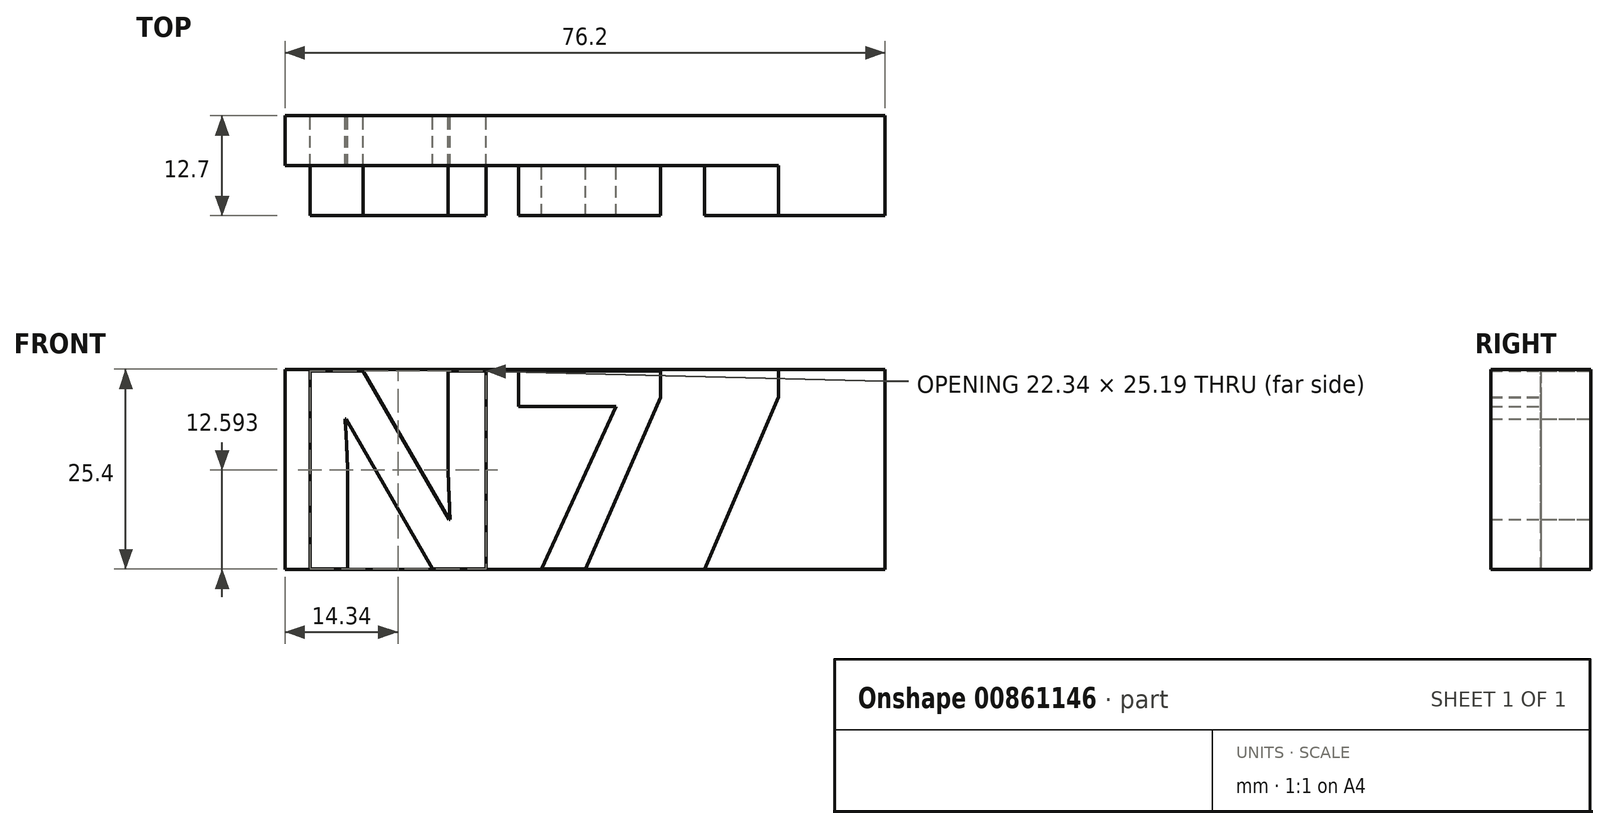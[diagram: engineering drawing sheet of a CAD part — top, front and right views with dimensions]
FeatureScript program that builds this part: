
annotation { "Feature Type Name" : "Feature", "Feature Type Description" : "" }
export const myFeature = defineFeature(function(context is Context, id is Id, definition is map)
    precondition{}
    {
        {
            var Q0;
            Q0=qCreatedBy(makeId("Front.planeOp"),FACE);
            var sketch = newSketch(context, id + "F0", { "sketchPlane" : qUnion([Q0])});
            skText(sketch, "E0", { "text": "N7", "fontName": "OpenSans-Bold.ttf"});
            skLineSegment(sketch, "E1.bottom", {"start": v(-29.76, 111.46) * mm, "end": v(46.44, 111.46) * mm});
            skLineSegment(sketch, "E1.top", {"start": v(-29.76, 86.06) * mm, "end": v(46.44, 86.06) * mm});
            skLineSegment(sketch, "E1.left", {"start": v(-29.76, 111.46) * mm, "end": v(-29.76, 86.06) * mm});
            skLineSegment(sketch, "E1.right", {"start": v(46.44, 111.46) * mm, "end": v(46.44, 86.06) * mm});
            skLineSegment(sketch, "E2", {"start": v(20.22, 111.46) * mm, "end": v(32.92, 111.46) * mm});
            skLineSegment(sketch, "E3", {"start": v(32.92, 111.46) * mm, "end": v(32.92, 107.96) * mm});
            skLineSegment(sketch, "E4", {"start": v(23.41, 85.79) * mm, "end": v(32.92, 107.96) * mm});
            skLineSegment(sketch, "E5", {"start": v(20.22, 86.06) * mm, "end": v(23.41, 85.79) * mm});
            const initialGuessF0  = {"E0": [-0.02976, 0.08606, 1, 0, 0.0254]};
            skSetInitialGuess(sketch, initialGuessF0);
            skSolve(sketch);
        }
        {
            var Q0;
            {var subQ1=sQuery(id+"F0.wireOp",EDGE,"E0.sketch_text.stroke-1");Q0=makeQuery(id+"F0.imprint","IMPRINT",FACE,{"disambiguationData":[TD([[makeQuery(id+"F0.imprint","IMPRINT",EDGE,{"derivedFrom":subQ1}),1.0]])]});}
            var Q1;
            {var subQ5=sQuery(id+"F0.wireOp",EDGE,"E0.sketch_text.stroke-6");Q1=makeQuery(id+"F0.imprint","IMPRINT",FACE,{"disambiguationData":[TD([[makeQuery(id+"F0.imprint","IMPRINT",EDGE,{"derivedFrom":subQ5}),1.0]])]});}
            extrude(context, id + "F1", {"entities" : qUnion([Q0, Q1]), "depth" : 6.35 * mm, "offsetDistance" : 25.4 * mm});
        }
        {
            var Q0;
            {var subQ1=sQuery(id+"F0.wireOp",EDGE,"E0.sketch_text.stroke-14");Q0=makeQuery(id+"F0.imprint","IMPRINT",FACE,{"disambiguationData":[TD([[makeQuery(id+"F0.imprint","IMPRINT",EDGE,{"derivedFrom":subQ1}),-1.0]])]});}
            extrude(context, id + "F2", {"entities" : qUnion([Q0]), "operationType" : NewBodyOperationType.ADD, "depth" : 12.7 * mm, "offsetDistance" : 25.4 * mm});
        }
        {
            var Q0;
            {var subQ1=sQuery(id+"F0.wireOp",EDGE,"E0.sketch_text.stroke-1");Q0=makeQuery(id+"F0.imprint","IMPRINT",FACE,{"disambiguationData":[TD([[makeQuery(id+"F0.imprint","IMPRINT",EDGE,{"derivedFrom":subQ1}),-1.0]])]});}
            extrude(context, id + "F3", {"entities" : qUnion([Q0]), "depth" : 12.7 * mm, "offsetDistance" : 25.4 * mm});
        }
        {
            var Q0;
            {var subQ1=sQuery(id+"F0.wireOp",EDGE,"E1.right");Q0=makeQuery(id+"F0.imprint","IMPRINT",FACE,{"disambiguationData":[TD([[makeQuery(id+"F0.imprint","IMPRINT",EDGE,{"derivedFrom":subQ1}),-1.0]])]});}
            extrude(context, id + "F4", {"entities" : qUnion([Q0]), "operationType" : NewBodyOperationType.ADD, "depth" : 12.7 * mm, "offsetDistance" : 25.4 * mm});
        }
    });
